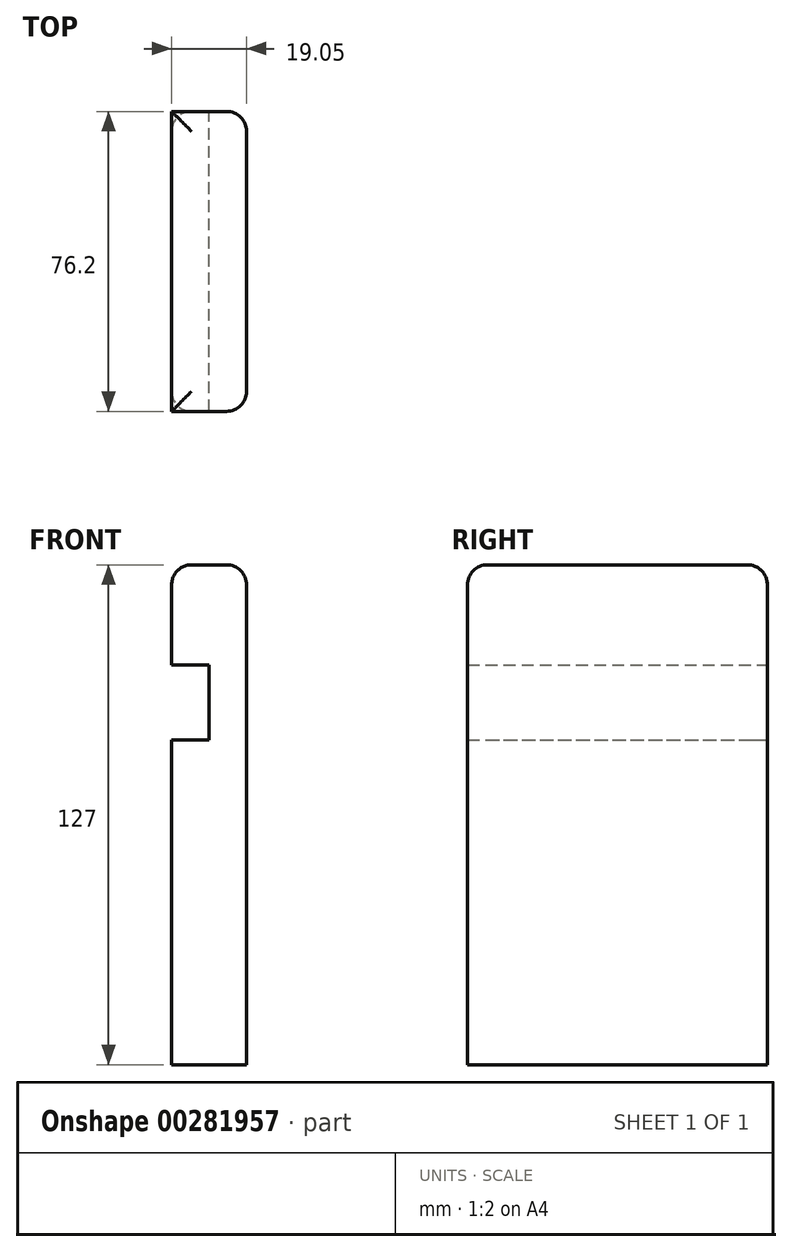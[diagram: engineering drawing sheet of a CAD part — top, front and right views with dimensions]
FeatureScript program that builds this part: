
annotation { "Feature Type Name" : "Feature", "Feature Type Description" : "" }
export const myFeature = defineFeature(function(context is Context, id is Id, definition is map)
    precondition{}
    {
        {
            var Q0;
            Q0=qCreatedBy(makeId("Front.planeOp"),FACE);
            var sketch = newSketch(context, id + "F0", { "sketchPlane" : qUnion([Q0])});
            skLineSegment(sketch, "E0", {"start": v(0, 0) * mm, "end": v(0, 127) * mm});
            skLineSegment(sketch, "E1", {"start": v(0, 127) * mm, "end": v(-19.05, 127) * mm});
            skLineSegment(sketch, "E2", {"start": v(-19.05, 127) * mm, "end": v(-19.05, 101.6) * mm});
            skLineSegment(sketch, "E3", {"start": v(-19.05, 101.6) * mm, "end": v(-9.52, 101.6) * mm});
            skLineSegment(sketch, "E4", {"start": v(-9.52, 101.6) * mm, "end": v(-9.52, 82.55) * mm});
            skLineSegment(sketch, "E5", {"start": v(-9.52, 82.55) * mm, "end": v(-19.05, 82.55) * mm});
            skLineSegment(sketch, "E6", {"start": v(-19.05, 82.55) * mm, "end": v(-19.05, 0) * mm});
            skLineSegment(sketch, "E7", {"start": v(-19.05, 0) * mm, "end": v(0, 0) * mm});
            skSolve(sketch);
        }
        {
            var Q0;
            Q0 = qSketchRegion(id + "F0", true);
            extrude(context, id + "F1", {"entities" : qUnion([Q0]), "depth" : 76.2 * mm});
        }
        {
            var Q0;
            Q0=makeQuery(id+"F1.opExtrude","SWEPT_EDGE",EDGE,{"disambiguationData":[OSD([sQuery(id+"F0.wireOp",EDGE,"E0"),sQuery(id+"F0.wireOp",EDGE,"E1")])]});
            var Q1;
            Q1=makeQuery(id+"F1.opExtrude","CAP_EDGE",EDGE,{"disambiguationData":[OSD([sQuery(id+"F0.wireOp",EDGE,"E0")])],"isStart":false});
            var Q2;
            Q2=makeQuery(id+"F1.opExtrude","CAP_EDGE",EDGE,{"disambiguationData":[OSD([sQuery(id+"F0.wireOp",EDGE,"E1")])],"isStart":false});
            var Q3;
            Q3=makeQuery(id+"F1.opExtrude","CAP_EDGE",EDGE,{"disambiguationData":[OSD([sQuery(id+"F0.wireOp",EDGE,"E6")])],"isStart":false});
            var Q4;
            Q4=makeQuery(id+"F1.opExtrude","CAP_EDGE",EDGE,{"disambiguationData":[OSD([sQuery(id+"F0.wireOp",EDGE,"E6")])],"isStart":true});
            var Q5;
            Q5=makeQuery(id+"F1.opExtrude","SWEPT_EDGE",EDGE,{"disambiguationData":[OSD([sQuery(id+"F0.wireOp",EDGE,"E1"),sQuery(id+"F0.wireOp",EDGE,"E2")])]});
            var Q6;
            Q6=makeQuery(id+"F1.opExtrude","CAP_EDGE",EDGE,{"disambiguationData":[OSD([sQuery(id+"F0.wireOp",EDGE,"E1")])],"isStart":true});
            var Q7;
            Q7=makeQuery(id+"F1.opExtrude","CAP_EDGE",EDGE,{"disambiguationData":[OSD([sQuery(id+"F0.wireOp",EDGE,"E0")])],"isStart":true});
            fillet(context, id + "F2", {"entities" : qUnion([Q0, Q1, Q2, Q3, Q4, Q5, Q6, Q7]), "radius" : 5.08 * mm, "tangentPropagation" : true, "allowEdgeOverflow" : false});
        }
    });
